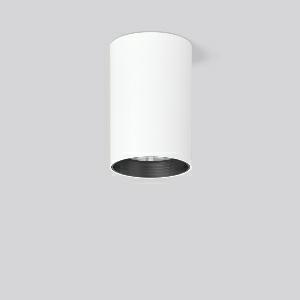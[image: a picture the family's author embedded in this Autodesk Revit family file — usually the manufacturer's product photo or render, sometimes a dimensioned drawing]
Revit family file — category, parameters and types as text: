
# Revit family: heledon_maxi_a_931228_002_fc3b
name_source: partatom
category: Lighting Fixtures
units: mm (PartAtom-declared; Revit-internal decimal feet)

## family parameters
Cut with Voids When Loaded = No
Host = Face
Light Source = No
Part Type = Normal
Room Calculation Point = No
Round Connector Dimension = Use Diameter
Shared = No

## types (1)
- HELEDON maxi A (1 x LED Modul 930, 3500 lm, 3000)
    Apparent Load = 35 VA
    Approval mark = CE
    CIE Flux Codes = 96 100 100 100 100
    Color Rendering = 90
    Color Temperature = 3000
    Default Elevation = 1800 mm
    Description = Series: HELEDON maxi
Cylindrical surface-mounted downlight. Housing: die-cast aluminium, powder-coated. Internal ceiling frame polycarbonate with bayonet mounting. Black plastic ring and recessed LED to prevent glare from the side. Optical assembly with lens made of plastic (polycarbonate) for the best homogeneous light distribution - can be changed without tools. Best colour rendering index Ra>90. Suitable for Ceiling mounting. Easy installation with a separate ceiling frame with bayonet mounting and plug connection. Driver integrated. Connected via plug-in connector. High quality converter without flickering and stroboscopic effect. The following accessories can be mounted without use of tools: interchangeable lenses, decorative glasses, honeycomb louvre, clear and frosted diffusers, white interchangeable plastic ring. 
Colour: traffic white, matt (RAL 9016)
Diameter: 123 mm
Height: 183 mm
Lamp: LED
Socket: without socket
Colour temperature: 3000K
Colour rendering index (CRI): 92
System power: 35 W
Rated luminous flux: 3500 lm
Luminous efficiency: 100 lm/W
Control gear: Regulated power supply
Protection class: I
Type of protection: IP 20
    Height = 183 mm
    Lamp = 1 x LED Modul 930
    Lamp Light Flux = 3500 lm
    Lamp count = 1
    Length = 123 mm
    Lifetime = 50000 h
    Luminous efficacy = 100 lm/W
    Manufacturer = RZB
    ModVariant = No
    Model = 931228.002
    Mounting Place = Ceiling
    Mounting Type = Surface mounted
    Number of Poles = 1
    OnlyDefault = Yes
    Power Factor = 1
    Product Name = HELEDON maxi A
    Product group = Surface mounted downlights
    ProductGroupID = 302
    Protection Class = Protection class I
    Protection Degree = IP 20
    RLX_Detail_Level = 1
    RLX_Emergency_Light_Flux = 0 lm
    RLX_Emergency_Type = 0
    RLX_Emergency_Type_DB = No
    RlxData = <blob elided: 97657 chars, md5=7e001ecc>
    Socket = socket
    Standby Power = 0 W
    System Light Flux = 3500 lm
    System Power = 35 W
    Type Comments = Product without accessories
    Type Image = 931193.002.jpg
    URL = http://relux.com
    VarID = ---
    Voltage = 230 V
    Voltage Range = 220-240 V
    Weight = 0.00 kg
    Width = 0 mm  [stored 0 ft]

note: [stored X ft] marks values corroborated as IEEE doubles in the binary element streams (Revit-internal decimal feet)

## geometry (parser evidence)
native form markers: Blend x4, Sweep x11
no freeform markers — native parametric forms only
